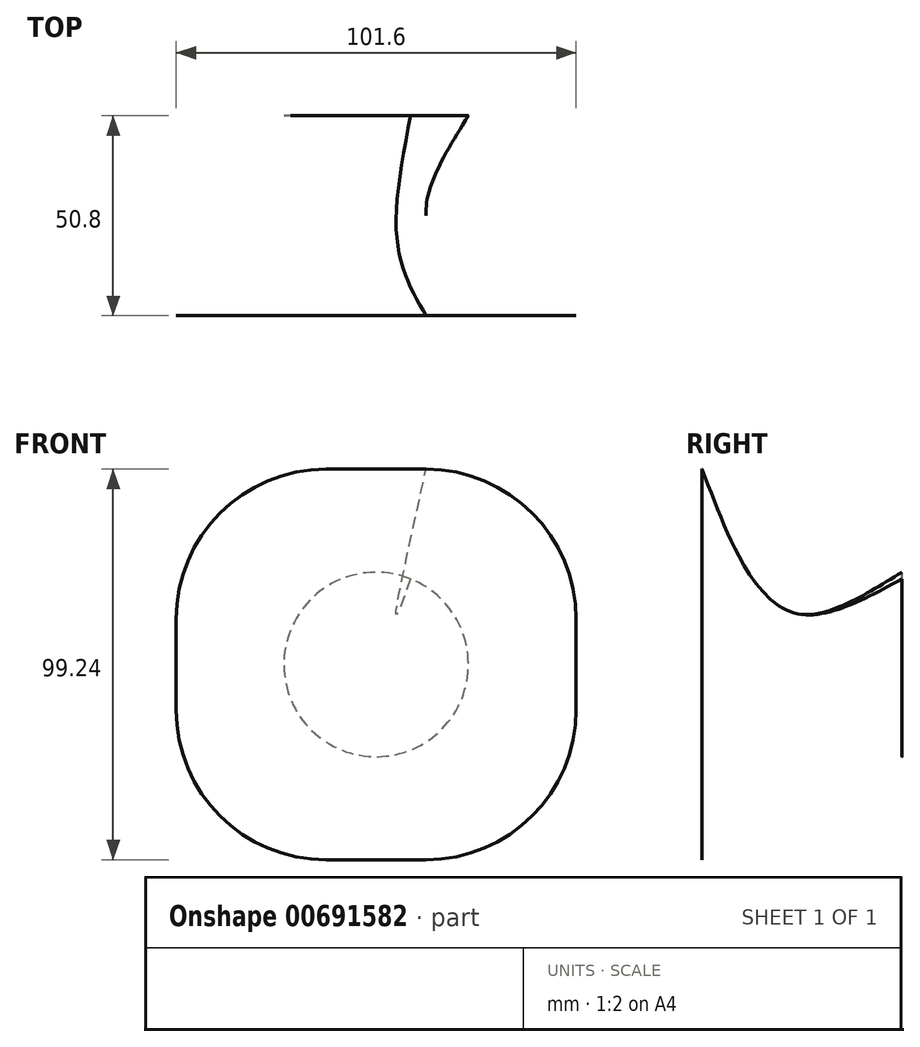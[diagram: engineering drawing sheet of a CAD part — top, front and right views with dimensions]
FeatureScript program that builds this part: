
annotation { "Feature Type Name" : "Feature", "Feature Type Description" : "" }
export const myFeature = defineFeature(function(context is Context, id is Id, definition is map)
    precondition{}
    {
        {
            var Q0;
            Q0=qCreatedBy(makeId("Front.planeOp"),FACE);
            var sketch = newSketch(context, id + "F0", { "sketchPlane" : qUnion([Q0])});
            skCircle(sketch, "E0", {"center": v(0, 0) * mm, "radius": 23.43 * mm});
            skSolve(sketch);
        }
        {
            var Q0;
            Q0=qCreatedBy(makeId("Front.planeOp"),FACE);
            cPlane(context, id + "F1", {"entities" : qUnion([Q0]), "cplaneType" : CPlaneType.OFFSET, "offset" : 50.8 * mm, "width" : 152.4 * mm, "height" : 152.4 * mm});
        }
        {
            var Q0;
            Q0=qCreatedBy(id+"F1.planeOp",FACE);
            var sketch = newSketch(context, id + "F2", { "sketchPlane" : qUnion([Q0])});
            skLineSegment(sketch, "E1.bottom", {"start": v(-12.7, 49.62) * mm, "end": v(12.7, 49.62) * mm});
            skLineSegment(sketch, "E1.top", {"start": v(-12.7, -49.62) * mm, "end": v(12.7, -49.62) * mm});
            skLineSegment(sketch, "E1.left", {"start": v(-50.8, 11.52) * mm, "end": v(-50.8, -11.52) * mm});
            skLineSegment(sketch, "E1.right", {"start": v(50.8, 11.52) * mm, "end": v(50.8, -11.52) * mm});
            skPoint(sketch, "E1.middle", {"position": v(0, 0) * mm});
            skPoint(sketch, "E2.visualSharp", {"position": v(-50.8, 49.62) * mm});
            skArc(sketch, "E2.filletArc", {"start": v(-12.7, 49.62) * mm, "mid": v(-39.64, 38.46) * mm, "end": v(-50.8, 11.52) * mm});
            skPoint(sketch, "E3.visualSharp", {"position": v(-50.8, -49.62) * mm});
            skArc(sketch, "E3.filletArc", {"start": v(-50.8, -11.52) * mm, "mid": v(-39.64, -38.46) * mm, "end": v(-12.7, -49.62) * mm});
            skPoint(sketch, "E4.visualSharp", {"position": v(50.8, 49.62) * mm});
            skArc(sketch, "E4.filletArc", {"start": v(50.8, 11.52) * mm, "mid": v(39.64, 38.46) * mm, "end": v(12.7, 49.62) * mm});
            skPoint(sketch, "E5.visualSharp", {"position": v(50.8, -49.62) * mm});
            skArc(sketch, "E5.filletArc", {"start": v(12.7, -49.62) * mm, "mid": v(39.64, -38.46) * mm, "end": v(50.8, -11.52) * mm});
            skSolve(sketch);
        }
        {
            var Q0;
            Q0=makeQuery(id+"F0.imprint","IMPRINT",FACE,{"disambiguationData":[TD([[makeQuery(id+"F0.imprint","IMPRINT",EDGE,{"derivedFrom":sQuery(id+"F0.wireOp",EDGE,"E0")}),1.0]])]});
            cPlane(context, id + "F3", {"entities" : qUnion([Q0]), "cplaneType" : CPlaneType.OFFSET, "offset" : 25.4 * mm, "width" : 152.4 * mm, "height" : 152.4 * mm});
        }
        {
            var Q0;
            Q0=qCreatedBy(id+"F3.planeOp",FACE);
            var sketch = newSketch(context, id + "F4", { "sketchPlane" : qUnion([Q0])});
            skPoint(sketch, "E6.middle", {"position": v(0, 0) * mm});
            skPoint(sketch, "E7.visualSharp", {"position": v(38.1, -38.1) * mm});
            skPoint(sketch, "E8.visualSharp", {"position": v(-38.1, 38.1) * mm});
            skPoint(sketch, "E9.visualSharp", {"position": v(38.1, 38.1) * mm});
            skLineSegment(sketch, "E10.bottom", {"start": v(5.08, 12.7) * mm, "end": v(-5.08, 12.7) * mm});
            skLineSegment(sketch, "E10.top", {"start": v(5.08, -12.7) * mm, "end": v(-5.08, -12.7) * mm});
            skLineSegment(sketch, "E10.left", {"start": v(12.7, 5.08) * mm, "end": v(12.7, -5.08) * mm});
            skLineSegment(sketch, "E10.right", {"start": v(-12.7, 5.08) * mm, "end": v(-12.7, -5.08) * mm});
            skPoint(sketch, "E11.visualSharp", {"position": v(-12.7, -12.7) * mm});
            skArc(sketch, "E11.filletArc", {"start": v(-12.7, -5.08) * mm, "mid": v(-10.47, -10.47) * mm, "end": v(-5.08, -12.7) * mm});
            skPoint(sketch, "E12.visualSharp", {"position": v(12.7, -12.7) * mm});
            skArc(sketch, "E12.filletArc", {"start": v(5.08, -12.7) * mm, "mid": v(10.47, -10.47) * mm, "end": v(12.7, -5.08) * mm});
            skPoint(sketch, "E13.visualSharp", {"position": v(-12.7, 12.7) * mm});
            skArc(sketch, "E13.filletArc", {"start": v(-5.08, 12.7) * mm, "mid": v(-10.47, 10.47) * mm, "end": v(-12.7, 5.08) * mm});
            skPoint(sketch, "E14.visualSharp", {"position": v(12.7, 12.7) * mm});
            skArc(sketch, "E14.filletArc", {"start": v(12.7, 5.08) * mm, "mid": v(10.47, 10.47) * mm, "end": v(5.08, 12.7) * mm});
            skSolve(sketch);
        }
        {
            var Q0;
            Q0=makeQuery(id+"F0.imprint","IMPRINT",FACE,{"disambiguationData":[TD([[makeQuery(id+"F0.imprint","IMPRINT",EDGE,{"derivedFrom":sQuery(id+"F0.wireOp",EDGE,"E0")}),1.0]])]});
            var Q1;
            Q1=makeQuery(id+"F4.imprint","IMPRINT",FACE,{"disambiguationData":[TD([[makeQuery(id+"F4.imprint","IMPRINT",EDGE,{"derivedFrom":sQuery(id+"F4.wireOp",EDGE,"E10.bottom")}),1.0]])]});
            var Q2;
            Q2=makeQuery(id+"F2.imprint","IMPRINT",FACE,{"disambiguationData":[TD([[makeQuery(id+"F2.imprint","IMPRINT",EDGE,{"derivedFrom":sQuery(id+"F2.wireOp",EDGE,"E1.bottom")}),-1.0]])]});
            loft(context, id + "F5", {"sheetProfilesArray" : [{ "sheetProfileEntities" : qUnion([Q0]) }, { "sheetProfileEntities" : qUnion([Q1]) }, { "sheetProfileEntities" : qUnion([Q2]) }]});
        }
    });
